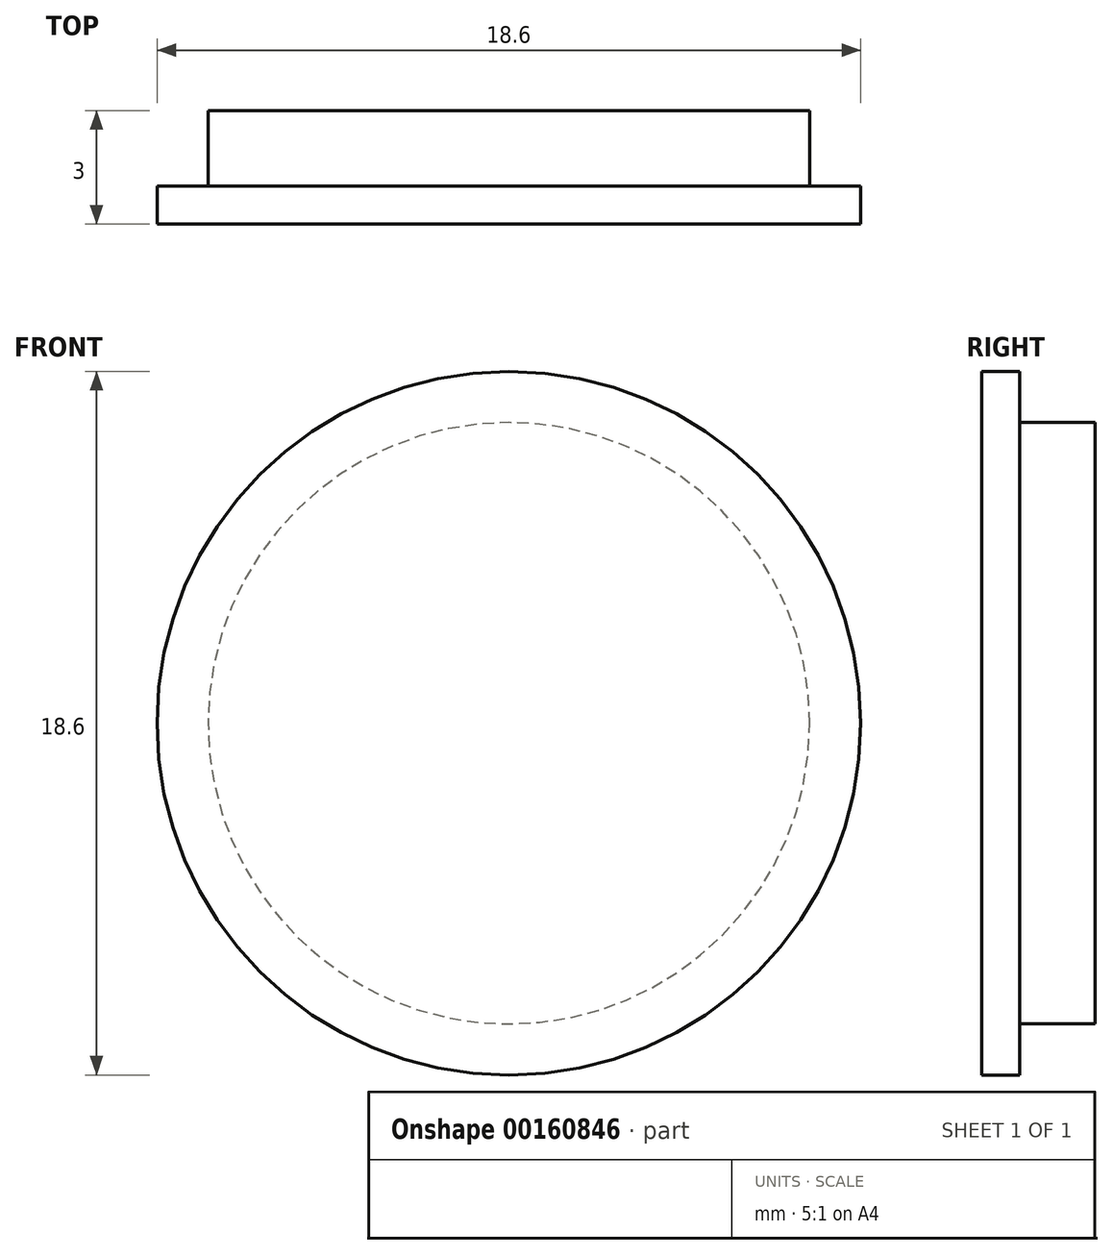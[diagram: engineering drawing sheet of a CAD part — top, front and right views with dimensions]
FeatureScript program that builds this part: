
annotation { "Feature Type Name" : "Feature", "Feature Type Description" : "" }
export const myFeature = defineFeature(function(context is Context, id is Id, definition is map)
    precondition{}
    {
        {
            var Q0;
            Q0=qCreatedBy(makeId("Right.planeOp"),FACE);
            var sketch = newSketch(context, id + "F0", { "sketchPlane" : qUnion([Q0])});
            skLineSegment(sketch, "E0", {"start": v(11.47, 0) * mm, "end": v(0, 0) * mm, "construction": true});
            skLineSegment(sketch, "E1", {"start": v(3, 0) * mm, "end": v(3, 7.95) * mm});
            skLineSegment(sketch, "E2", {"start": v(1, 7.95) * mm, "end": v(3, 7.95) * mm});
            skLineSegment(sketch, "E3", {"start": v(1, 7.95) * mm, "end": v(1, 9.3) * mm});
            skLineSegment(sketch, "E4", {"start": v(0, 9.3) * mm, "end": v(1, 9.3) * mm});
            skLineSegment(sketch, "E5", {"start": v(0, 9.3) * mm, "end": v(0, 0) * mm});
            skLineSegment(sketch, "E6", {"start": v(3, 0) * mm, "end": v(0, 0) * mm});
            skSolve(sketch);
        }
        {
            var Q0;
            Q0=makeQuery(id+"F0.imprint","IMPRINT",FACE,{"disambiguationData":[TD([[makeQuery(id+"F0.imprint","IMPRINT",EDGE,{"derivedFrom":sQuery(id+"F0.wireOp",EDGE,"E1")}),1.0]])]});
            var Q1;
            Q1=sQuery(id+"F0.wireOp",EDGE,"E0");
            revolve(context, id + "F1", {"entities" : qUnion([Q0]), "axis" : qUnion([Q1]), "revolveType" : RevolveType.FULL});
        }
    });
